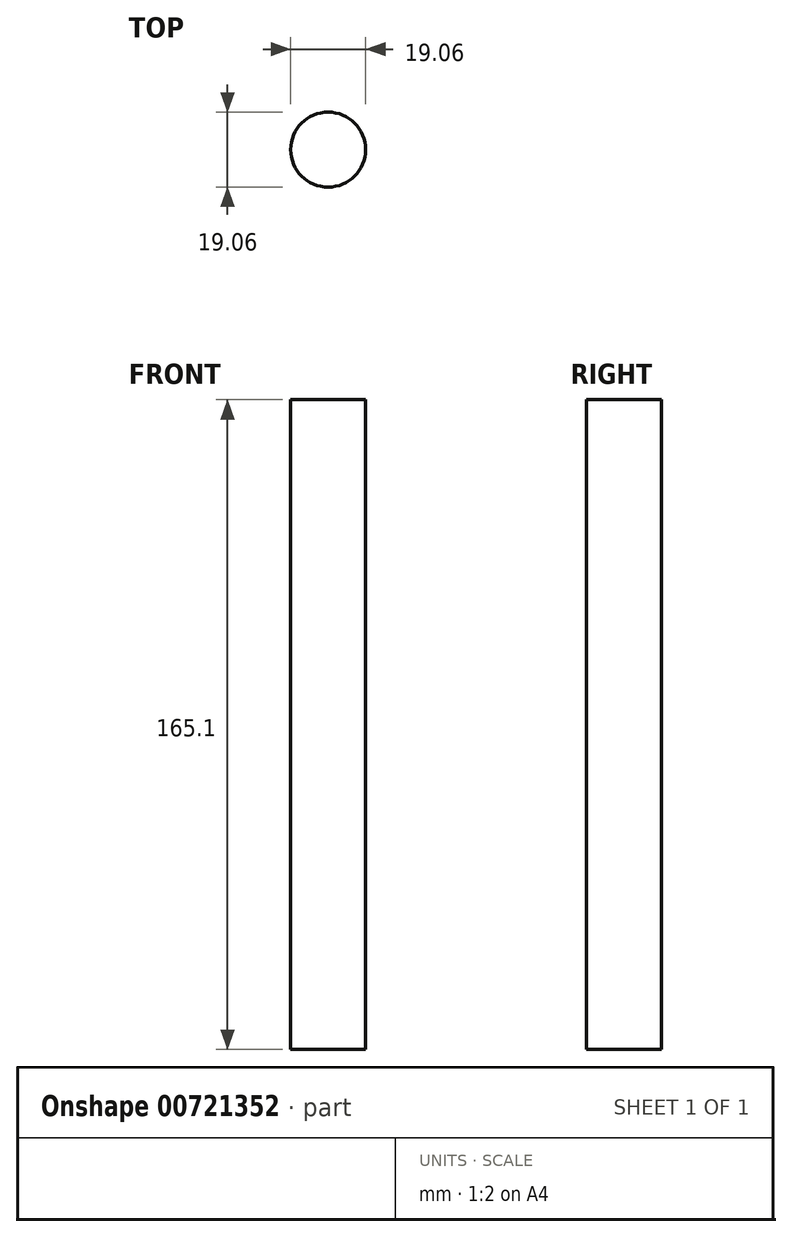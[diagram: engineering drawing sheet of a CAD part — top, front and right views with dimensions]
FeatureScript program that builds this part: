
annotation { "Feature Type Name" : "Feature", "Feature Type Description" : "" }
export const myFeature = defineFeature(function(context is Context, id is Id, definition is map)
    precondition{}
    {
        {
            var Q0;
            Q0=qCreatedBy(makeId("Top.planeOp"),FACE);
            var sketch = newSketch(context, id + "F0", { "sketchPlane" : qUnion([Q0])});
            skCircle(sketch, "E0", {"center": v(0, 0) * mm, "radius": 9.53 * mm});
            skSolve(sketch);
        }
        {
            var Q0;
            Q0 = qSketchRegion(id + "F0", true);
            extrude(context, id + "F1", {"entities" : qUnion([Q0]), "depth" : 165.1 * mm, "offsetDistance" : 25.4 * mm});
        }
    });
